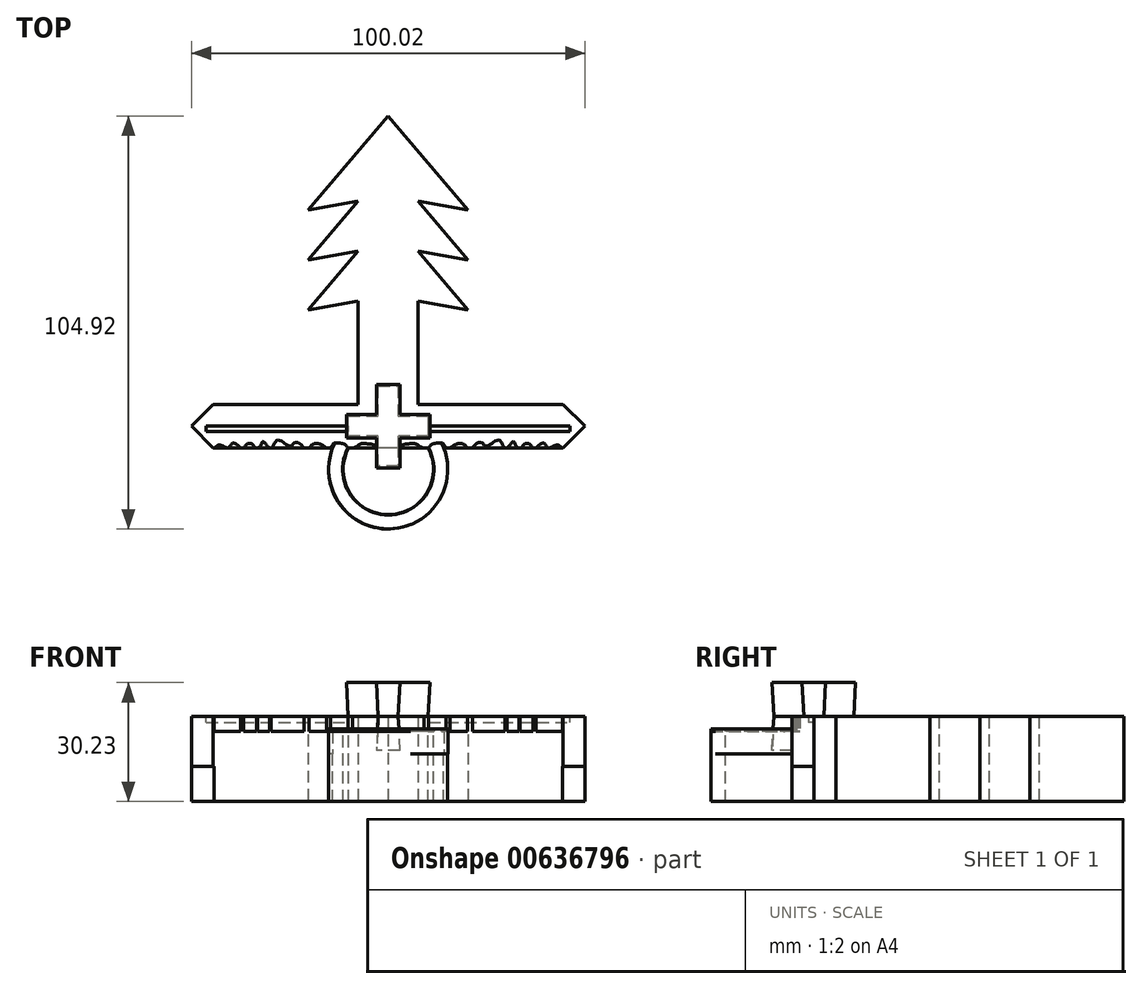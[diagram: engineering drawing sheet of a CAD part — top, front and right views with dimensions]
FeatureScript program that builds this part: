
annotation { "Feature Type Name" : "Feature", "Feature Type Description" : "" }
export const myFeature = defineFeature(function(context is Context, id is Id, definition is map)
    precondition{}
    {
        {
            var Q0;
            Q0=qCreatedBy(makeId("Top.planeOp"),FACE);
            var sketch = newSketch(context, id + "F0", { "sketchPlane" : qUnion([Q0])});
            skLineSegment(sketch, "E0", {"start": v(0, 93.4) * mm, "end": v(0, -5.78) * mm, "construction": true});
            skLineSegment(sketch, "E1", {"start": v(0, 0) * mm, "end": v(-7.62, 0) * mm});
            skLineSegment(sketch, "E2", {"start": v(-7.62, 0) * mm, "end": v(-7.62, 31.75) * mm});
            skLineSegment(sketch, "E3", {"start": v(-7.62, 31.75) * mm, "end": v(-20.32, 29.51) * mm});
            skLineSegment(sketch, "E4", {"start": v(-20.32, 29.51) * mm, "end": v(-7.62, 44.45) * mm});
            skLineSegment(sketch, "E5", {"start": v(-7.62, 44.45) * mm, "end": v(-20.32, 42.21) * mm});
            skLineSegment(sketch, "E6", {"start": v(-20.32, 42.21) * mm, "end": v(-7.62, 57.15) * mm});
            skLineSegment(sketch, "E7", {"start": v(-7.62, 57.15) * mm, "end": v(-20.32, 54.91) * mm});
            skLineSegment(sketch, "E8", {"start": v(-20.32, 54.91) * mm, "end": v(0, 78.81) * mm});
            skLineSegment(sketch, "E9", {"start": v(-7.62, 0) * mm, "end": v(-7.62, 82.36) * mm, "construction": true});
            skLineSegment(sketch, "E10", {"start": v(-20.32, 67.05) * mm, "end": v(-20.32, 0) * mm, "construction": true});
            skPoint(sketch, "E11", {"position": v(-7.62, 69.85) * mm});
            skLineSegment(sketch, "E12.MirrorCS", {"start": v(20.32, 54.91) * mm, "end": v(0, 78.81) * mm});
            skLineSegment(sketch, "E13.MirrorCS", {"start": v(7.62, 57.15) * mm, "end": v(20.32, 54.91) * mm});
            skLineSegment(sketch, "E14.MirrorCS", {"start": v(20.32, 42.21) * mm, "end": v(7.62, 57.15) * mm});
            skLineSegment(sketch, "E15.MirrorCS", {"start": v(7.62, 44.45) * mm, "end": v(20.32, 42.21) * mm});
            skLineSegment(sketch, "E16.MirrorCS", {"start": v(20.32, 29.51) * mm, "end": v(7.62, 44.45) * mm});
            skLineSegment(sketch, "E17.MirrorCS", {"start": v(7.62, 31.75) * mm, "end": v(20.32, 29.51) * mm});
            skLineSegment(sketch, "E18.MirrorCS", {"start": v(7.62, 0) * mm, "end": v(7.62, 31.75) * mm});
            skLineSegment(sketch, "E19.MirrorCS", {"start": v(0, 0) * mm, "end": v(7.62, 0) * mm});
            skSolve(sketch);
        }
        {
            var Q0;
            Q0 = qSketchRegion(id + "F0", true);
            extrude(context, id + "F1", {"entities" : qUnion([Q0]), "depth" : 12.7 * mm, "offsetDistance" : 25.4 * mm});
        }
        {
            var Q0;
            Q0=qCreatedBy(makeId("Top.planeOp"),FACE);
            cPlane(context, id + "F2", {"entities" : qUnion([Q0]), "cplaneType" : CPlaneType.OFFSET, "offset" : 6.35 * mm, "width" : 152.4 * mm, "height" : 152.4 * mm});
        }
        {
            var Q0;
            Q0=qCreatedBy(id+"F2.planeOp",FACE);
            var sketch = newSketch(context, id + "F3", { "sketchPlane" : qUnion([Q0])});
            skArc(sketch, "E20", {"start": v(0, -15.24) * mm, "mid": v(15.24, 0) * mm, "end": v(0, 15.24) * mm});
            skLineSegment(sketch, "E21", {"start": v(0, 15.24) * mm, "end": v(0, -15.24) * mm});
            skLineSegment(sketch, "E22", {"start": v(0, 24.9) * mm, "end": v(0, -24.18) * mm, "construction": true});
            skSolve(sketch);
        }
        {
            var Q0;
            Q0=sQuery(id+"F3.wireOp",EDGE,"E20");
            var Q1;
            Q1=sQuery(id+"F3.wireOp",EDGE,"E22");
            revolve(context, id + "F4", {"bodyType" : ToolBodyType.SURFACE, "surfaceEntities" : qUnion([Q0]), "axis" : qUnion([Q1]), "revolveType" : RevolveType.FULL});
        }
        {
            var Q0;
            Q0=qCreatedBy(id+"F2.planeOp",FACE);
            var sketch = newSketch(context, id + "F5", { "sketchPlane" : qUnion([Q0])});
            skLineSegment(sketch, "E23", {"start": v(0, -57.2) * mm, "end": v(0, 36.37) * mm, "construction": true});
            skLineSegment(sketch, "E24.bottom", {"start": v(0, 5.56) * mm, "end": v(44.45, 5.56) * mm});
            skLineSegment(sketch, "E24.top", {"start": v(0, -5.56) * mm, "end": v(44.45, -5.56) * mm});
            skLineSegment(sketch, "E24.left", {"start": v(0, 5.56) * mm, "end": v(0, -5.56) * mm});
            skLineSegment(sketch, "E25", {"start": v(44.45, 5.56) * mm, "end": v(50, 0) * mm});
            skLineSegment(sketch, "E26", {"start": v(50, 0) * mm, "end": v(44.45, -5.56) * mm});
            skLineSegment(sketch, "E27.MirrorCS", {"start": v(0, 5.56) * mm, "end": v(-44.45, 5.56) * mm});
            skLineSegment(sketch, "E28.MirrorCS", {"start": v(-44.45, 5.56) * mm, "end": v(-50, 0) * mm});
            skLineSegment(sketch, "E29.MirrorCS", {"start": v(-50, 0) * mm, "end": v(-44.45, -5.56) * mm});
            skLineSegment(sketch, "E30.MirrorCS", {"start": v(0, -5.56) * mm, "end": v(-44.45, -5.56) * mm});
            skSolve(sketch);
        }
        {
            var Q0;
            Q0 = qSketchRegion(id + "F5", true);
            extrude(context, id + "F6", {"entities" : qUnion([Q0]), "operationType" : NewBodyOperationType.ADD, "endBound" : BoundingType.SYMMETRIC, "depth" : 12.7 * mm, "offsetDistance" : 25.4 * mm});
        }
        {
            var Q0;
            Q0 = qSketchRegion(id + "F5", true);
            extrude(context, id + "F7", {"entities" : qUnion([Q0]), "operationType" : NewBodyOperationType.ADD, "endBound" : BoundingType.SYMMETRIC, "depth" : 12.7 * mm, "offsetDistance" : 25.4 * mm});
        }
        {
            var Q0;
            Q0=qCreatedBy(id+"F2.planeOp",FACE);
            var sketch = newSketch(context, id + "F8", { "sketchPlane" : qUnion([Q0])});
            skLineSegment(sketch, "E31", {"start": v(-47.23, -2.78) * mm, "end": v(47.23, -2.78) * mm, "construction": true});
            skLineSegment(sketch, "E32", {"start": v(-47.23, -2.78) * mm, "end": v(-44.09, -15.46) * mm});
            skLineSegment(sketch, "E33", {"start": v(-44.09, -15.46) * mm, "end": v(44.12, -15.46) * mm});
            skLineSegment(sketch, "E34", {"start": v(44.12, -15.46) * mm, "end": v(47.23, -2.78) * mm});
            skFitSpline(sketch, "E35", {"points": [v(47.23, -2.78) * mm, v(44.5, -5.62) * mm, v(42.9, -4.73) * mm, v(40.74, -5.53) * mm, v(39.67, -4.37) * mm, v(38.23, -4.82) * mm, v(37.07, -5.8) * mm, v(35.9, -4.55) * mm, v(34.56, -4.55) * mm, v(33.75, -5.45) * mm, v(32.68, -5.27) * mm, v(31.87, -3.92) * mm, v(30.88, -4.82) * mm, v(29.9, -5.62) * mm, v(29, -4.64) * mm, v(28.46, -3.74) * mm, v(27.57, -3.56) * mm, v(26.4, -4.28) * mm, v(25.24, -5) * mm, v(24.43, -4.9) * mm, v(23.9, -4.2) * mm, v(22.55, -4.37) * mm, v(21.38, -5.53) * mm, v(20.49, -5.8) * mm, v(19.77, -5.09) * mm, v(18.7, -4.37) * mm, v(16.9, -4.73) * mm, v(15.1, -5.71) * mm, v(14.21, -4.9) * mm, v(13.94, -4.37) * mm, v(12.42, -4.28) * mm, v(10.72, -4.82) * mm, v(10.27, -5.53) * mm, v(8.03, -5.18) * mm, v(6.95, -4.46) * mm, v(0, -5.53) * mm], "startDerivative": vector(-62.99, -95.82) * mm, "endDerivative": vector(-142.4, -33.8) * mm});
            skFitSpline(sketch, "E36.MirrorCS", {"points": [v(-47.23, -2.78) * mm, v(-44.5, -5.62) * mm, v(-42.9, -4.73) * mm, v(-40.74, -5.53) * mm, v(-39.67, -4.37) * mm, v(-38.23, -4.82) * mm, v(-37.07, -5.8) * mm, v(-35.9, -4.55) * mm, v(-34.56, -4.55) * mm, v(-33.75, -5.45) * mm, v(-32.68, -5.27) * mm, v(-31.87, -3.92) * mm, v(-30.88, -4.82) * mm, v(-29.9, -5.62) * mm, v(-29, -4.64) * mm, v(-28.46, -3.74) * mm, v(-27.57, -3.56) * mm, v(-26.4, -4.28) * mm, v(-25.24, -5) * mm, v(-24.43, -4.9) * mm, v(-23.9, -4.2) * mm, v(-22.55, -4.37) * mm, v(-21.38, -5.53) * mm, v(-20.49, -5.8) * mm, v(-19.77, -5.09) * mm, v(-18.7, -4.37) * mm, v(-16.9, -4.73) * mm, v(-15.1, -5.71) * mm, v(-14.21, -4.9) * mm, v(-13.94, -4.37) * mm, v(-12.42, -4.28) * mm, v(-10.72, -4.82) * mm, v(-10.27, -5.53) * mm, v(-8.03, -5.18) * mm, v(-6.95, -4.46) * mm, v(0, -5.53) * mm], "startDerivative": vector(62.99, -95.82) * mm, "endDerivative": vector(142.4, -33.8) * mm});
            skSolve(sketch);
        }
        {
            var Q0;
            Q0 = qSketchRegion(id + "F8", true);
            extrude(context, id + "F9", {"entities" : qUnion([Q0]), "operationType" : NewBodyOperationType.REMOVE, "endBound" : BoundingType.SYMMETRIC, "oppositeDirection" : true, "depth" : 25.4 * mm, "offsetDistance" : 25.4 * mm});
        }
        {
            var Q0;
            Q0=makeQuery(id+"F6.boolean.opBoolean","MERGE",FACE,{"derivedFrom":[makeQuery(id+"F1.opExtrude","CAP_FACE",FACE,{"disambiguationData":[OSD([sQuery(id+"F0.wireOp",EDGE,"E1"),sQuery(id+"F0.wireOp",EDGE,"E2"),sQuery(id+"F0.wireOp",EDGE,"E3"),sQuery(id+"F0.wireOp",EDGE,"E4"),sQuery(id+"F0.wireOp",EDGE,"E5"),sQuery(id+"F0.wireOp",EDGE,"E6"),sQuery(id+"F0.wireOp",EDGE,"E7"),sQuery(id+"F0.wireOp",EDGE,"E8"),sQuery(id+"F0.wireOp",EDGE,"E12.MirrorCS"),sQuery(id+"F0.wireOp",EDGE,"E13.MirrorCS"),sQuery(id+"F0.wireOp",EDGE,"E14.MirrorCS"),sQuery(id+"F0.wireOp",EDGE,"E15.MirrorCS"),sQuery(id+"F0.wireOp",EDGE,"E16.MirrorCS"),sQuery(id+"F0.wireOp",EDGE,"E17.MirrorCS"),sQuery(id+"F0.wireOp",EDGE,"E18.MirrorCS"),sQuery(id+"F0.wireOp",EDGE,"E19.MirrorCS")])],"isStart":false}),makeQuery(id+"F6.opExtrude","CAP_FACE",FACE,{"disambiguationData":[OSD([sQuery(id+"F5.wireOp",EDGE,"E24.bottom"),sQuery(id+"F5.wireOp",EDGE,"E24.top"),sQuery(id+"F5.wireOp",EDGE,"E25"),sQuery(id+"F5.wireOp",EDGE,"E26"),sQuery(id+"F5.wireOp",EDGE,"E27.MirrorCS"),sQuery(id+"F5.wireOp",EDGE,"E28.MirrorCS"),sQuery(id+"F5.wireOp",EDGE,"E29.MirrorCS"),sQuery(id+"F5.wireOp",EDGE,"E30.MirrorCS")])],"isStart":false})]});
            var sketch = newSketch(context, id + "F10", { "sketchPlane" : qUnion([Q0])});
            skLineSegment(sketch, "E37.bottom", {"start": v(-46.25, 0) * mm, "end": v(46.15, 0) * mm});
            skLineSegment(sketch, "E37.top", {"start": v(-46.25, -1.32) * mm, "end": v(46.15, -1.32) * mm});
            skLineSegment(sketch, "E37.left", {"start": v(-46.25, 0) * mm, "end": v(-46.25, -1.32) * mm});
            skLineSegment(sketch, "E37.right", {"start": v(46.15, 0) * mm, "end": v(46.15, -1.32) * mm});
            skSolve(sketch);
        }
        {
            var Q0;
            Q0 = qSketchRegion(id + "F10", true);
            extrude(context, id + "F11", {"entities" : qUnion([Q0]), "operationType" : NewBodyOperationType.REMOVE, "oppositeDirection" : true, "depth" : 1.52 * mm, "offsetDistance" : 25.4 * mm});
        }
        {
            var Q0;
            Q0=qCreatedBy(id+"F2.planeOp",FACE);
            var sketch = newSketch(context, id + "F12", { "sketchPlane" : qUnion([Q0])});
            skCircle(sketch, "E38", {"center": v(0, -10.96) * mm, "radius": 15.12 * mm});
            skCircle(sketch, "E39", {"center": v(0, -10.96) * mm, "radius": 11.6 * mm});
            skSolve(sketch);
        }
        {
            var Q0;
            Q0 = qSketchRegion(id + "F12", true);
            extrude(context, id + "F13", {"entities" : qUnion([Q0]), "operationType" : NewBodyOperationType.ADD, "endBound" : BoundingType.SYMMETRIC, "depth" : 6.35 * mm, "offsetDistance" : 25.4 * mm});
        }
        {
            var Q0;
            Q0=makeQuery(id+"F6.boolean.opBoolean","MERGE",FACE,{"derivedFrom":[makeQuery(id+"F1.opExtrude","CAP_FACE",FACE,{"disambiguationData":[OSD([sQuery(id+"F0.wireOp",EDGE,"E1"),sQuery(id+"F0.wireOp",EDGE,"E2"),sQuery(id+"F0.wireOp",EDGE,"E3"),sQuery(id+"F0.wireOp",EDGE,"E4"),sQuery(id+"F0.wireOp",EDGE,"E5"),sQuery(id+"F0.wireOp",EDGE,"E6"),sQuery(id+"F0.wireOp",EDGE,"E7"),sQuery(id+"F0.wireOp",EDGE,"E8"),sQuery(id+"F0.wireOp",EDGE,"E12.MirrorCS"),sQuery(id+"F0.wireOp",EDGE,"E13.MirrorCS"),sQuery(id+"F0.wireOp",EDGE,"E14.MirrorCS"),sQuery(id+"F0.wireOp",EDGE,"E15.MirrorCS"),sQuery(id+"F0.wireOp",EDGE,"E16.MirrorCS"),sQuery(id+"F0.wireOp",EDGE,"E17.MirrorCS"),sQuery(id+"F0.wireOp",EDGE,"E18.MirrorCS"),sQuery(id+"F0.wireOp",EDGE,"E19.MirrorCS")])],"isStart":false}),makeQuery(id+"F6.opExtrude","CAP_FACE",FACE,{"disambiguationData":[OSD([sQuery(id+"F5.wireOp",EDGE,"E24.bottom"),sQuery(id+"F5.wireOp",EDGE,"E24.top"),sQuery(id+"F5.wireOp",EDGE,"E25"),sQuery(id+"F5.wireOp",EDGE,"E26"),sQuery(id+"F5.wireOp",EDGE,"E27.MirrorCS"),sQuery(id+"F5.wireOp",EDGE,"E28.MirrorCS"),sQuery(id+"F5.wireOp",EDGE,"E29.MirrorCS"),sQuery(id+"F5.wireOp",EDGE,"E30.MirrorCS")])],"isStart":false})]});
            var sketch = newSketch(context, id + "F14", { "sketchPlane" : qUnion([Q0])});
            skLineSegment(sketch, "E40", {"start": v(0, 10.16) * mm, "end": v(2.54, 10.16) * mm});
            skLineSegment(sketch, "E41", {"start": v(2.54, 10.16) * mm, "end": v(2.54, 2.54) * mm});
            skLineSegment(sketch, "E42", {"start": v(2.54, 2.54) * mm, "end": v(10.16, 2.54) * mm});
            skLineSegment(sketch, "E43", {"start": v(10.16, 2.54) * mm, "end": v(10.16, 0) * mm});
            skLineSegment(sketch, "E44.MirrorCS", {"start": v(0, 10.16) * mm, "end": v(-2.54, 10.16) * mm});
            skLineSegment(sketch, "E45.MirrorCS", {"start": v(-2.54, 10.16) * mm, "end": v(-2.54, 2.54) * mm});
            skLineSegment(sketch, "E46.MirrorCS", {"start": v(-10.16, 2.54) * mm, "end": v(-10.16, 0) * mm});
            skLineSegment(sketch, "E47.MirrorCS", {"start": v(-2.54, 2.54) * mm, "end": v(-10.16, 2.54) * mm});
            skLineSegment(sketch, "E48.MirrorCS", {"start": v(-10.16, -2.54) * mm, "end": v(-10.16, 0) * mm});
            skLineSegment(sketch, "E49.MirrorCS", {"start": v(-2.54, -2.54) * mm, "end": v(-10.16, -2.54) * mm});
            skLineSegment(sketch, "E50.MirrorCS", {"start": v(-2.54, -10.16) * mm, "end": v(-2.54, -2.54) * mm});
            skLineSegment(sketch, "E51.MirrorCS", {"start": v(0, -10.16) * mm, "end": v(-2.54, -10.16) * mm});
            skLineSegment(sketch, "E52.MirrorCS", {"start": v(0, -10.16) * mm, "end": v(2.54, -10.16) * mm});
            skLineSegment(sketch, "E53.MirrorCS", {"start": v(2.54, -10.16) * mm, "end": v(2.54, -2.54) * mm});
            skLineSegment(sketch, "E54.MirrorCS", {"start": v(2.54, -2.54) * mm, "end": v(10.16, -2.54) * mm});
            skLineSegment(sketch, "E55.MirrorCS", {"start": v(10.16, -2.54) * mm, "end": v(10.16, 0) * mm});
            skSolve(sketch);
        }
        {
            var Q0;
            Q0 = qSketchRegion(id + "F14", true);
            extrude(context, id + "F15", {"entities" : qUnion([Q0]), "operationType" : NewBodyOperationType.ADD, "endBound" : BoundingType.SYMMETRIC, "depth" : 17.27 * mm, "offsetDistance" : 25.4 * mm, "hasDraft" : true, "draftAngle" : 3 * degree});
        }
        {
            var Q0;
            Q0=makeQuery(id+"F6.boolean.opBoolean","MERGE",FACE,{"derivedFrom":[makeQuery(id+"F1.opExtrude","CAP_FACE",FACE,{"disambiguationData":[OSD([sQuery(id+"F0.wireOp",EDGE,"E1"),sQuery(id+"F0.wireOp",EDGE,"E2"),sQuery(id+"F0.wireOp",EDGE,"E3"),sQuery(id+"F0.wireOp",EDGE,"E4"),sQuery(id+"F0.wireOp",EDGE,"E5"),sQuery(id+"F0.wireOp",EDGE,"E6"),sQuery(id+"F0.wireOp",EDGE,"E7"),sQuery(id+"F0.wireOp",EDGE,"E8"),sQuery(id+"F0.wireOp",EDGE,"E12.MirrorCS"),sQuery(id+"F0.wireOp",EDGE,"E13.MirrorCS"),sQuery(id+"F0.wireOp",EDGE,"E14.MirrorCS"),sQuery(id+"F0.wireOp",EDGE,"E15.MirrorCS"),sQuery(id+"F0.wireOp",EDGE,"E16.MirrorCS"),sQuery(id+"F0.wireOp",EDGE,"E17.MirrorCS"),sQuery(id+"F0.wireOp",EDGE,"E18.MirrorCS"),sQuery(id+"F0.wireOp",EDGE,"E19.MirrorCS")])],"isStart":true}),makeQuery(id+"F6.opExtrude","CAP_FACE",FACE,{"disambiguationData":[OSD([sQuery(id+"F5.wireOp",EDGE,"E24.bottom"),sQuery(id+"F5.wireOp",EDGE,"E24.top"),sQuery(id+"F5.wireOp",EDGE,"E25"),sQuery(id+"F5.wireOp",EDGE,"E26"),sQuery(id+"F5.wireOp",EDGE,"E27.MirrorCS"),sQuery(id+"F5.wireOp",EDGE,"E28.MirrorCS"),sQuery(id+"F5.wireOp",EDGE,"E29.MirrorCS"),sQuery(id+"F5.wireOp",EDGE,"E30.MirrorCS")])],"isStart":true})]});
            var sketch = newSketch(context, id + "F16", { "sketchPlane" : qUnion([Q0])});
            skLineSegment(sketch, "E56", {"start": v(0, -78.81) * mm, "end": v(20.32, -54.91) * mm});
            skLineSegment(sketch, "E57", {"start": v(20.32, -54.91) * mm, "end": v(7.62, -57.15) * mm});
            skLineSegment(sketch, "E58", {"start": v(7.62, -57.15) * mm, "end": v(20.32, -42.21) * mm});
            skLineSegment(sketch, "E59", {"start": v(20.32, -42.21) * mm, "end": v(7.62, -44.45) * mm});
            skLineSegment(sketch, "E60", {"start": v(7.62, -44.45) * mm, "end": v(20.32, -29.51) * mm});
            skLineSegment(sketch, "E61", {"start": v(20.32, -29.51) * mm, "end": v(7.62, -31.75) * mm});
            skLineSegment(sketch, "E62", {"start": v(7.62, -31.75) * mm, "end": v(7.62, -5.56) * mm});
            skLineSegment(sketch, "E63", {"start": v(7.62, -5.56) * mm, "end": v(44.45, -5.56) * mm});
            skLineSegment(sketch, "E64", {"start": v(44.45, -5.56) * mm, "end": v(50, 0) * mm});
            skLineSegment(sketch, "E65", {"start": v(50, 0) * mm, "end": v(44.28, 5.56) * mm});
            skLineSegment(sketch, "E66", {"start": v(44.28, 5.56) * mm, "end": v(13.98, 5.56) * mm});
            skLineSegment(sketch, "E67", {"start": v(-44.28, 5.56) * mm, "end": v(-50, 0) * mm});
            skLineSegment(sketch, "E68", {"start": v(-50, 0) * mm, "end": v(-44.45, -5.56) * mm});
            skLineSegment(sketch, "E69", {"start": v(-44.45, -5.56) * mm, "end": v(-7.62, -5.56) * mm});
            skLineSegment(sketch, "E70", {"start": v(-7.62, -5.56) * mm, "end": v(-7.62, -31.75) * mm});
            skLineSegment(sketch, "E71", {"start": v(-7.62, -31.75) * mm, "end": v(-20.32, -29.51) * mm});
            skLineSegment(sketch, "E72", {"start": v(-20.32, -29.51) * mm, "end": v(-7.62, -44.45) * mm});
            skLineSegment(sketch, "E73", {"start": v(-7.62, -44.45) * mm, "end": v(-20.32, -42.21) * mm});
            skLineSegment(sketch, "E74", {"start": v(-20.32, -42.21) * mm, "end": v(-7.62, -57.15) * mm});
            skLineSegment(sketch, "E75", {"start": v(-7.62, -57.15) * mm, "end": v(-20.32, -54.91) * mm});
            skLineSegment(sketch, "E76", {"start": v(-20.32, -54.91) * mm, "end": v(0, -78.81) * mm});
            skArc(sketch, "E77", {"start": v(13.98, 5.56) * mm, "mid": v(-0.07, 26.11) * mm, "end": v(-14.12, 5.56) * mm});
            skPoint(sketch, "E77.first.point", {"position": v(-14.28, 16.07) * mm});
            skPoint(sketch, "E77.second.point", {"position": v(9.84, 22.4) * mm});
            skPoint(sketch, "E77.third.point", {"position": v(14.66, 14.26) * mm});
            skArc(sketch, "E78", {"start": v(10.14, 5.56) * mm, "mid": v(0.02, 22.46) * mm, "end": v(-10.1, 5.56) * mm});
            skPoint(sketch, "E78.first.point", {"position": v(-8.4, 18.79) * mm});
            skPoint(sketch, "E78.second.point", {"position": v(6.52, 20.44) * mm});
            skPoint(sketch, "E78.third.point", {"position": v(11.5, 11.25) * mm});
            skLineSegment(sketch, "E79.trimOffspring", {"start": v(-14.12, 5.56) * mm, "end": v(-44.28, 5.56) * mm});
            skLineSegment(sketch, "E80", {"start": v(10.23, 5.56) * mm, "end": v(-10.1, 5.56) * mm});
            skSolve(sketch);
        }
        {
            var Q0;
            Q0 = qSketchRegion(id + "F16", true);
            extrude(context, id + "F17", {"entities" : qUnion([Q0]), "operationType" : NewBodyOperationType.ADD, "endBound" : BoundingType.SYMMETRIC, "depth" : 17.78 * mm, "offsetDistance" : 25.4 * mm});
        }
    });
